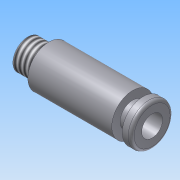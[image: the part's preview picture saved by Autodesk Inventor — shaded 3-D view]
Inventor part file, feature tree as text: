
AUTODESK INVENTOR PART (.ipt)
format: ipt  version: 2012 SP1 (Build 160190100, 190)  size: 123,904 bytes
history: native  units: mm
features: revolve x1, thread x1, fillet x1, sketch x1
ambient origin geometry x8: Origin, YZ Plane, XZ Plane, XY Plane, X Axis, Y Axis, Z Axis, Center Point
bodies: Volumenkörper1 (feature_tree)
feature tree (4):
  revolve  "Umdrehung1"
  thread  "Gewinde1"  [1 undecoded]
  fillet  "Rundung1"  Radius=3.5mm
  sketch  "Skizze1"  dims[d2=2.5mm d3=2.1mm d4=1.5mm d5=1.75mm d6=14.0mm d7=3.5mm d8=90.0deg d9=10.0mm d10=0.0mm d11=1.75mm d12=13.0mm d13=0.5mm]
note: 1 required parameter value undecoded (feature->parameter linkage not recoverable at this tier; creation-order binding heuristic only, values carry confidence <= 0.55)
